# Revit family: Legrand Flush-mounting cabinets
name_source: partatom
category: Installations électriques
units: mm (PartAtom-declared; Revit-internal decimal feet)

## family parameters
Basée sur le plan de construction = Non
Conserver l'orientation des annotations = Non
Cote de connecteur circulaire = Utiliser le diamètre
Couper avec des vides une fois chargée = Non
Numéro OmniClass = 23.80.00.00
Partagée = Non
Point de calcul de pièce = Non
Titre OmniClass = Electric Power and Lighting
Toujours verticalement = Oui
Type d'élément = Normal

## types (14) — shared parameters
Fabricant = Legrand
General Conditions of Use = https://export.legrand.com
Maximum permissible current = 63 A
Modèle = Flush-mounting cabinet
URL = www.legrand.com
zero-valued in all types: Elévation par défaut

## per-type parameters (varying)
- Flush-mounting cabinet 8 modules Plastic door 001410: Assembly Plastic door 1R=Non; Assembly Plastic door 1R 8M=Oui; Assembly Plastic door 2R=Non; Assembly Plastic door 3R=Non; Assembly Plastic door 4R=Non; Assembly Plastic door transparent 1R=Non; Assembly Plastic door transparent 1R 8M=Non; Assembly Plastic door transparent 2R=Non; Assembly Plastic door transparent 3R=Non; Assembly Plastic door transparent 4R=Non; Assembly metal door 1R=Non; Assembly metal door 2R=Non; Assembly metal door 3R=Non; Assembly metal door 4R=Non; Cabinet 001410=Oui; Cabinet 001420=Non; Cabinet 001511=Non; Cabinet 001512=Non; Cabinet 001513=Non; Cabinet 001514=Non; Cabinet 001521=Non; Cabinet 001522=Non; Cabinet 001523=Non; Cabinet 001524=Non; Cabinet 001531=Non; Cabinet 001532=Non; Cabinet 001533=Non; Cabinet 001534=Non; Number of modules per row=8; Number of rows=1; Plastic door=Oui; Recessed depth=73 mm  [stored 0.239501 ft]; Recessed height=213 mm  [stored 0.698819 ft]; Recessed width=205 mm  [stored 0.672572 ft]; Terminal block E=8 connections Icc 10kA; height=228 mm  [stored 0.748031 ft]; metal door=Non; transparent door=Non; width=245 mm  [stored 0.803806 ft]
- Flush-mounting cabinet 8 modules transparent door 001420: Assembly Plastic door 1R=Non; Assembly Plastic door 1R 8M=Non; Assembly Plastic door 2R=Non; Assembly Plastic door 3R=Non; Assembly Plastic door 4R=Non; Assembly Plastic door transparent 1R=Non; Assembly Plastic door transparent 1R 8M=Oui; Assembly Plastic door transparent 2R=Non; Assembly Plastic door transparent 3R=Non; Assembly Plastic door transparent 4R=Non; Assembly metal door 1R=Non; Assembly metal door 2R=Non; Assembly metal door 3R=Non; Assembly metal door 4R=Non; Cabinet 001410=Non; Cabinet 001420=Oui; Cabinet 001511=Non; Cabinet 001512=Non; Cabinet 001513=Non; Cabinet 001514=Non; Cabinet 001521=Non; Cabinet 001522=Non; Cabinet 001523=Non; Cabinet 001524=Non; Cabinet 001531=Non; Cabinet 001532=Non; Cabinet 001533=Non; Cabinet 001534=Non; Number of modules per row=8; Number of rows=1; Plastic door=Non; Recessed depth=73 mm  [stored 0.239501 ft]; Recessed height=213 mm  [stored 0.698819 ft]; Recessed width=205 mm  [stored 0.672572 ft]; Terminal block E=8 connections Icc 10kA; height=228 mm  [stored 0.748031 ft]; metal door=Non; transparent door=Oui; width=245 mm  [stored 0.803806 ft]
- Flush-mounting cabinet 12 modules Plastic door 001511: Assembly Plastic door 1R=Oui; Assembly Plastic door 1R 8M=Non; Assembly Plastic door 2R=Non; Assembly Plastic door 3R=Non; Assembly Plastic door 4R=Non; Assembly Plastic door transparent 1R=Non; Assembly Plastic door transparent 1R 8M=Non; Assembly Plastic door transparent 2R=Non; Assembly Plastic door transparent 3R=Non; Assembly Plastic door transparent 4R=Non; Assembly metal door 1R=Non; Assembly metal door 2R=Non; Assembly metal door 3R=Non; Assembly metal door 4R=Non; Cabinet 001410=Non; Cabinet 001420=Non; Cabinet 001511=Oui; Cabinet 001512=Non; Cabinet 001513=Non; Cabinet 001514=Non; Cabinet 001521=Non; Cabinet 001522=Non; Cabinet 001523=Non; Cabinet 001524=Non; Cabinet 001531=Non; Cabinet 001532=Non; Cabinet 001533=Non; Cabinet 001534=Non; Number of modules per row=12+2; Number of rows=1; Plastic door=Oui; Recessed depth=90 mm  [stored 0.295276 ft]; Recessed height=305 mm  [stored 1.00066 ft]; Recessed width=330 mm; Terminal block E=automatic connection terminal block 5+9 holes Icc 10kA; height=335 mm  [stored 1.09908 ft]; metal door=Non; transparent door=Non; width=350 mm  [stored 1.14829 ft]
- Flush-mounting cabinet 24 modules Plastic door 001512: Assembly Plastic door 1R=Non; Assembly Plastic door 1R 8M=Non; Assembly Plastic door 2R=Oui; Assembly Plastic door 3R=Non; Assembly Plastic door 4R=Non; Assembly Plastic door transparent 1R=Non; Assembly Plastic door transparent 1R 8M=Non; Assembly Plastic door transparent 2R=Non; Assembly Plastic door transparent 3R=Non; Assembly Plastic door transparent 4R=Non; Assembly metal door 1R=Non; Assembly metal door 2R=Non; Assembly metal door 3R=Non; Assembly metal door 4R=Non; Cabinet 001410=Non; Cabinet 001420=Non; Cabinet 001511=Non; Cabinet 001512=Oui; Cabinet 001513=Non; Cabinet 001514=Non; Cabinet 001521=Non; Cabinet 001522=Non; Cabinet 001523=Non; Cabinet 001524=Non; Cabinet 001531=Non; Cabinet 001532=Non; Cabinet 001533=Non; Cabinet 001534=Non; Number of modules per row=12+2; Number of rows=2; Plastic door=Oui; Recessed depth=90 mm  [stored 0.295276 ft]; Recessed height=430 mm; Recessed width=330 mm; Terminal block E=automatic connection terminal block 5+18 holes Icc 10kA; height=460 mm  [stored 1.50919 ft]; metal door=Non; transparent door=Non; width=350 mm  [stored 1.14829 ft]
- Flush-mounting cabinet 36 modules Plastic door 001513: Assembly Plastic door 1R=Non; Assembly Plastic door 1R 8M=Non; Assembly Plastic door 2R=Non; Assembly Plastic door 3R=Oui; Assembly Plastic door 4R=Non; Assembly Plastic door transparent 1R=Non; Assembly Plastic door transparent 1R 8M=Non; Assembly Plastic door transparent 2R=Non; Assembly Plastic door transparent 3R=Non; Assembly Plastic door transparent 4R=Non; Assembly metal door 1R=Non; Assembly metal door 2R=Non; Assembly metal door 3R=Non; Assembly metal door 4R=Non; Cabinet 001410=Non; Cabinet 001420=Non; Cabinet 001511=Non; Cabinet 001512=Non; Cabinet 001513=Oui; Cabinet 001514=Non; Cabinet 001521=Non; Cabinet 001522=Non; Cabinet 001523=Non; Cabinet 001524=Non; Cabinet 001531=Non; Cabinet 001532=Non; Cabinet 001533=Non; Cabinet 001534=Non; Number of modules per row=12+2; Number of rows=3; Plastic door=Oui; Recessed depth=90 mm  [stored 0.295276 ft]; Recessed height=555 mm  [stored 1.82087 ft]; Recessed width=330 mm; Terminal block E=automatic connection terminal block 5+27 holes Icc 10kA; height=585 mm  [stored 1.91929 ft]; metal door=Non; transparent door=Non; width=350 mm  [stored 1.14829 ft]
- Flush-mounting cabinet 48 modules Plastic door 001514: Assembly Plastic door 1R=Non; Assembly Plastic door 1R 8M=Non; Assembly Plastic door 2R=Non; Assembly Plastic door 3R=Non; Assembly Plastic door 4R=Oui; Assembly Plastic door transparent 1R=Non; Assembly Plastic door transparent 1R 8M=Non; Assembly Plastic door transparent 2R=Non; Assembly Plastic door transparent 3R=Non; Assembly Plastic door transparent 4R=Non; Assembly metal door 1R=Non; Assembly metal door 2R=Non; Assembly metal door 3R=Non; Assembly metal door 4R=Non; Cabinet 001410=Non; Cabinet 001420=Non; Cabinet 001511=Non; Cabinet 001512=Non; Cabinet 001513=Non; Cabinet 001514=Oui; Cabinet 001521=Non; Cabinet 001522=Non; Cabinet 001523=Non; Cabinet 001524=Non; Cabinet 001531=Non; Cabinet 001532=Non; Cabinet 001533=Non; Cabinet 001534=Non; Number of modules per row=12+2; Number of rows=4; Plastic door=Oui; Recessed depth=90 mm  [stored 0.295276 ft]; Recessed height=680 mm  [stored 2.23097 ft]; Recessed width=330 mm; Terminal block E=automatic connection terminal block 5+36 holes Icc 10kA; height=710 mm  [stored 2.3294 ft]; metal door=Non; transparent door=Non; width=350 mm  [stored 1.14829 ft]
- Flush-mounting cabinet 12 modules transparent door 001521: Assembly Plastic door 1R=Non; Assembly Plastic door 1R 8M=Non; Assembly Plastic door 2R=Non; Assembly Plastic door 3R=Non; Assembly Plastic door 4R=Non; Assembly Plastic door transparent 1R=Oui; Assembly Plastic door transparent 1R 8M=Non; Assembly Plastic door transparent 2R=Non; Assembly Plastic door transparent 3R=Non; Assembly Plastic door transparent 4R=Non; Assembly metal door 1R=Non; Assembly metal door 2R=Non; Assembly metal door 3R=Non; Assembly metal door 4R=Non; Cabinet 001410=Non; Cabinet 001420=Non; Cabinet 001511=Non; Cabinet 001512=Non; Cabinet 001513=Non; Cabinet 001514=Non; Cabinet 001521=Oui; Cabinet 001522=Non; Cabinet 001523=Non; Cabinet 001524=Non; Cabinet 001531=Non; Cabinet 001532=Non; Cabinet 001533=Non; Cabinet 001534=Non; Number of modules per row=12+2; Number of rows=1; Plastic door=Non; Recessed depth=90 mm  [stored 0.295276 ft]; Recessed height=305 mm  [stored 1.00066 ft]; Recessed width=330 mm; Terminal block E=automatic connection terminal block 5+9 holes Icc 10kA; height=335 mm  [stored 1.09908 ft]; metal door=Non; transparent door=Oui; width=350 mm  [stored 1.14829 ft]
- Flush-mounting cabinet 24 modules transparent door 001522: Assembly Plastic door 1R=Non; Assembly Plastic door 1R 8M=Non; Assembly Plastic door 2R=Non; Assembly Plastic door 3R=Non; Assembly Plastic door 4R=Non; Assembly Plastic door transparent 1R=Non; Assembly Plastic door transparent 1R 8M=Non; Assembly Plastic door transparent 2R=Oui; Assembly Plastic door transparent 3R=Non; Assembly Plastic door transparent 4R=Non; Assembly metal door 1R=Non; Assembly metal door 2R=Non; Assembly metal door 3R=Non; Assembly metal door 4R=Non; Cabinet 001410=Non; Cabinet 001420=Non; Cabinet 001511=Non; Cabinet 001512=Non; Cabinet 001513=Non; Cabinet 001514=Non; Cabinet 001521=Non; Cabinet 001522=Oui; Cabinet 001523=Non; Cabinet 001524=Non; Cabinet 001531=Non; Cabinet 001532=Non; Cabinet 001533=Non; Cabinet 001534=Non; Number of modules per row=12+2; Number of rows=2; Plastic door=Non; Recessed depth=90 mm  [stored 0.295276 ft]; Recessed height=430 mm; Recessed width=330 mm; Terminal block E=automatic connection terminal block 5+18 holes Icc 10kA; height=460 mm  [stored 1.50919 ft]; metal door=Non; transparent door=Oui; width=350 mm  [stored 1.14829 ft]
- Flush-mounting cabinet 36 modules transparent door 001523: Assembly Plastic door 1R=Non; Assembly Plastic door 1R 8M=Non; Assembly Plastic door 2R=Non; Assembly Plastic door 3R=Non; Assembly Plastic door 4R=Non; Assembly Plastic door transparent 1R=Non; Assembly Plastic door transparent 1R 8M=Non; Assembly Plastic door transparent 2R=Non; Assembly Plastic door transparent 3R=Oui; Assembly Plastic door transparent 4R=Non; Assembly metal door 1R=Non; Assembly metal door 2R=Non; Assembly metal door 3R=Non; Assembly metal door 4R=Non; Cabinet 001410=Non; Cabinet 001420=Non; Cabinet 001511=Non; Cabinet 001512=Non; Cabinet 001513=Non; Cabinet 001514=Non; Cabinet 001521=Non; Cabinet 001522=Non; Cabinet 001523=Oui; Cabinet 001524=Non; Cabinet 001531=Non; Cabinet 001532=Non; Cabinet 001533=Non; Cabinet 001534=Non; Number of modules per row=12+2; Number of rows=3; Plastic door=Non; Recessed depth=90 mm  [stored 0.295276 ft]; Recessed height=555 mm  [stored 1.82087 ft]; Recessed width=330 mm; Terminal block E=automatic connection terminal block 5+27 holes Icc 10kA; height=585 mm  [stored 1.91929 ft]; metal door=Non; transparent door=Oui; width=350 mm  [stored 1.14829 ft]
- Flush-mounting cabinet 48 modules transparent door 001524: Assembly Plastic door 1R=Non; Assembly Plastic door 1R 8M=Non; Assembly Plastic door 2R=Non; Assembly Plastic door 3R=Non; Assembly Plastic door 4R=Non; Assembly Plastic door transparent 1R=Non; Assembly Plastic door transparent 1R 8M=Non; Assembly Plastic door transparent 2R=Non; Assembly Plastic door transparent 3R=Non; Assembly Plastic door transparent 4R=Oui; Assembly metal door 1R=Non; Assembly metal door 2R=Non; Assembly metal door 3R=Non; Assembly metal door 4R=Non; Cabinet 001410=Non; Cabinet 001420=Non; Cabinet 001511=Non; Cabinet 001512=Non; Cabinet 001513=Non; Cabinet 001514=Non; Cabinet 001521=Non; Cabinet 001522=Non; Cabinet 001523=Non; Cabinet 001524=Oui; Cabinet 001531=Non; Cabinet 001532=Non; Cabinet 001533=Non; Cabinet 001534=Non; Number of modules per row=12+2; Number of rows=4; Plastic door=Non; Recessed depth=90 mm  [stored 0.295276 ft]; Recessed height=680 mm  [stored 2.23097 ft]; Recessed width=330 mm; Terminal block E=automatic connection terminal block 5+36 holes Icc 10kA; height=710 mm  [stored 2.3294 ft]; metal door=Non; transparent door=Oui; width=350 mm  [stored 1.14829 ft]
- Flush-mounting cabinet 12 modules metal door 001531: Assembly Plastic door 1R=Non; Assembly Plastic door 1R 8M=Non; Assembly Plastic door 2R=Non; Assembly Plastic door 3R=Non; Assembly Plastic door 4R=Non; Assembly Plastic door transparent 1R=Non; Assembly Plastic door transparent 1R 8M=Non; Assembly Plastic door transparent 2R=Non; Assembly Plastic door transparent 3R=Non; Assembly Plastic door transparent 4R=Non; Assembly metal door 1R=Oui; Assembly metal door 2R=Non; Assembly metal door 3R=Non; Assembly metal door 4R=Non; Cabinet 001410=Non; Cabinet 001420=Non; Cabinet 001511=Non; Cabinet 001512=Non; Cabinet 001513=Non; Cabinet 001514=Non; Cabinet 001521=Non; Cabinet 001522=Non; Cabinet 001523=Non; Cabinet 001524=Non; Cabinet 001531=Oui; Cabinet 001532=Non; Cabinet 001533=Non; Cabinet 001534=Non; Number of modules per row=12+2; Number of rows=1; Plastic door=Non; Recessed depth=90 mm  [stored 0.295276 ft]; Recessed height=305 mm  [stored 1.00066 ft]; Recessed width=330 mm; Terminal block E=automatic connection terminal block 5+9 holes Icc 10kA; height=335 mm  [stored 1.09908 ft]; metal door=Oui; transparent door=Non; width=350 mm  [stored 1.14829 ft]
- Flush-mounting cabinet 24 modules metal door 001532: Assembly Plastic door 1R=Non; Assembly Plastic door 1R 8M=Non; Assembly Plastic door 2R=Non; Assembly Plastic door 3R=Non; Assembly Plastic door 4R=Non; Assembly Plastic door transparent 1R=Non; Assembly Plastic door transparent 1R 8M=Non; Assembly Plastic door transparent 2R=Non; Assembly Plastic door transparent 3R=Non; Assembly Plastic door transparent 4R=Non; Assembly metal door 1R=Non; Assembly metal door 2R=Oui; Assembly metal door 3R=Non; Assembly metal door 4R=Non; Cabinet 001410=Non; Cabinet 001420=Non; Cabinet 001511=Non; Cabinet 001512=Non; Cabinet 001513=Non; Cabinet 001514=Non; Cabinet 001521=Non; Cabinet 001522=Non; Cabinet 001523=Non; Cabinet 001524=Non; Cabinet 001531=Non; Cabinet 001532=Oui; Cabinet 001533=Non; Cabinet 001534=Non; Number of modules per row=12+2; Number of rows=2; Plastic door=Non; Recessed depth=90 mm  [stored 0.295276 ft]; Recessed height=430 mm; Recessed width=330 mm; Terminal block E=automatic connection terminal block 5+18 holes Icc 10kA; height=460 mm  [stored 1.50919 ft]; metal door=Oui; transparent door=Non; width=350 mm  [stored 1.14829 ft]
- Flush-mounting cabinet 36 modules metal door 001533: Assembly Plastic door 1R=Non; Assembly Plastic door 1R 8M=Non; Assembly Plastic door 2R=Non; Assembly Plastic door 3R=Non; Assembly Plastic door 4R=Non; Assembly Plastic door transparent 1R=Non; Assembly Plastic door transparent 1R 8M=Non; Assembly Plastic door transparent 2R=Non; Assembly Plastic door transparent 3R=Non; Assembly Plastic door transparent 4R=Non; Assembly metal door 1R=Non; Assembly metal door 2R=Non; Assembly metal door 3R=Oui; Assembly metal door 4R=Non; Cabinet 001410=Non; Cabinet 001420=Non; Cabinet 001511=Non; Cabinet 001512=Non; Cabinet 001513=Non; Cabinet 001514=Non; Cabinet 001521=Non; Cabinet 001522=Non; Cabinet 001523=Non; Cabinet 001524=Non; Cabinet 001531=Non; Cabinet 001532=Non; Cabinet 001533=Oui; Cabinet 001534=Non; Number of modules per row=12+2; Number of rows=3; Plastic door=Non; Recessed depth=90 mm  [stored 0.295276 ft]; Recessed height=555 mm  [stored 1.82087 ft]; Recessed width=330 mm; Terminal block E=automatic connection terminal block 5+27 holes Icc 10kA; height=585 mm  [stored 1.91929 ft]; metal door=Oui; transparent door=Non; width=350 mm  [stored 1.14829 ft]
- Flush-mounting cabinet 48 modules metal door 001534: Assembly Plastic door 1R=Non; Assembly Plastic door 1R 8M=Non; Assembly Plastic door 2R=Non; Assembly Plastic door 3R=Non; Assembly Plastic door 4R=Non; Assembly Plastic door transparent 1R=Non; Assembly Plastic door transparent 1R 8M=Non; Assembly Plastic door transparent 2R=Non; Assembly Plastic door transparent 3R=Non; Assembly Plastic door transparent 4R=Non; Assembly metal door 1R=Non; Assembly metal door 2R=Non; Assembly metal door 3R=Non; Assembly metal door 4R=Oui; Cabinet 001410=Non; Cabinet 001420=Non; Cabinet 001511=Non; Cabinet 001512=Non; Cabinet 001513=Non; Cabinet 001514=Non; Cabinet 001521=Non; Cabinet 001522=Non; Cabinet 001523=Non; Cabinet 001524=Non; Cabinet 001531=Non; Cabinet 001532=Non; Cabinet 001533=Non; Cabinet 001534=Oui; Number of modules per row=12+2; Number of rows=4; Plastic door=Non; Recessed depth=90 mm  [stored 0.295276 ft]; Recessed height=680 mm  [stored 2.23097 ft]; Recessed width=330 mm; Terminal block E=automatic connection terminal block 5+36 holes Icc 10kA; height=710 mm  [stored 2.3294 ft]; metal door=Oui; transparent door=Non; width=350 mm  [stored 1.14829 ft]

note: [stored X ft] marks values corroborated as IEEE doubles in the binary element streams (Revit-internal decimal feet)
